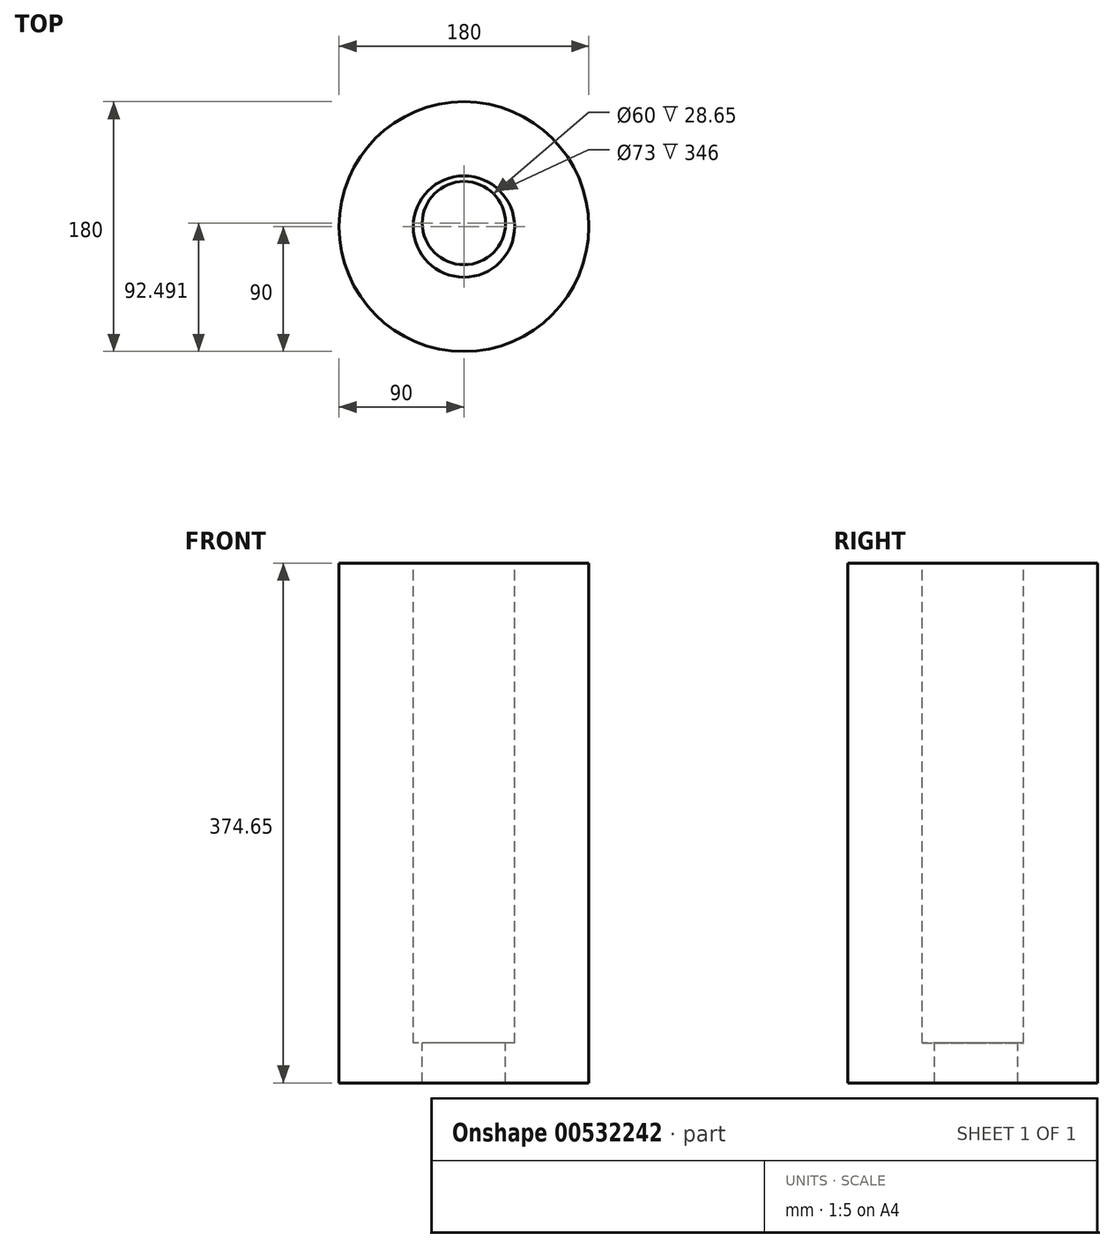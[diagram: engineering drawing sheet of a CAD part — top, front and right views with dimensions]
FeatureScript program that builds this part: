
annotation { "Feature Type Name" : "Feature", "Feature Type Description" : "" }
export const myFeature = defineFeature(function(context is Context, id is Id, definition is map)
    precondition{}
    {
        {
            var Q0;
            Q0=qCreatedBy(makeId("Front.planeOp"),FACE);
            var sketch = newSketch(context, id + "F0", { "sketchPlane" : qUnion([Q0])});
            skLineSegment(sketch, "E0", {"start": v(0, 0) * mm, "end": v(0, -374.65) * mm});
            skLineSegment(sketch, "E1", {"start": v(0, -374.65) * mm, "end": v(90, -374.65) * mm});
            skLineSegment(sketch, "E2", {"start": v(90, 0) * mm, "end": v(0, 0) * mm});
            skLineSegment(sketch, "E3", {"start": v(0, 0) * mm, "end": v(0, 0) * mm});
            skLineSegment(sketch, "E4", {"start": v(90, -374.65) * mm, "end": v(90, 0) * mm});
            skSolve(sketch);
        }
        {
            var Q0;
            Q0=makeQuery(id+"F0.imprint","IMPRINT",FACE,{"disambiguationData":[TD([[makeQuery(id+"F0.imprint","IMPRINT",EDGE,{"derivedFrom":sQuery(id+"F0.wireOp",EDGE,"E0")}),1.0]])]});
            var Q1;
            Q1=sQuery(id+"F0.wireOp",EDGE,"E0");
            revolve(context, id + "F1", {"entities" : qUnion([Q0]), "axis" : qUnion([Q1]), "revolveType" : RevolveType.FULL});
        }
        {
            var Q0;
            Q0=makeQuery(id+"F1.opRevolve","SWEPT_FACE",FACE,{"disambiguationData":[OSD([sQuery(id+"F0.wireOp",EDGE,"E2")])]});
            var sketch = newSketch(context, id + "F2", { "sketchPlane" : qUnion([Q0])});
            skCircle(sketch, "E5", {"center": v(0, 2.5) * mm, "radius": 30 * mm});
            skSolve(sketch);
        }
        {
            var Q0;
            Q0=makeQuery(id+"F2.imprint","IMPRINT",FACE,{"disambiguationData":[TD([[makeQuery(id+"F2.imprint","IMPRINT",EDGE,{"derivedFrom":sQuery(id+"F2.wireOp",EDGE,"E5")}),1.0]])]});
            var Q1;
            Q1=sQuery(id+"F2.wireOp",EDGE,"E5");
            extrude(context, id + "F3", {"entities" : qUnion([Q0]), "operationType" : NewBodyOperationType.REMOVE, "surfaceEntities" : qUnion([Q1]), "endBound" : BoundingType.THROUGH_ALL, "oppositeDirection" : true, "depth" : 25.4 * mm, "offsetDistance" : 25.4 * mm});
        }
        {
            var Q0;
            Q0=makeQuery(id+"F1.opRevolve","SWEPT_FACE",FACE,{"disambiguationData":[OSD([sQuery(id+"F0.wireOp",EDGE,"E2")])]});
            var sketch = newSketch(context, id + "F4", { "sketchPlane" : qUnion([Q0])});
            skCircle(sketch, "E6", {"center": v(0, 0) * mm, "radius": 36.5 * mm});
            skSolve(sketch);
        }
        {
            var Q0;
            Q0=makeQuery(id+"F4.imprint","IMPRINT",FACE,{"disambiguationData":[TD([[makeQuery(id+"F4.imprint","IMPRINT",EDGE,{"derivedFrom":sQuery(id+"F4.wireOp",EDGE,"E6")}),1.0]])]});
            extrude(context, id + "F5", {"entities" : qUnion([Q0]), "operationType" : NewBodyOperationType.REMOVE, "oppositeDirection" : true, "depth" : 346 * mm, "offsetDistance" : 25.4 * mm});
        }
    });
